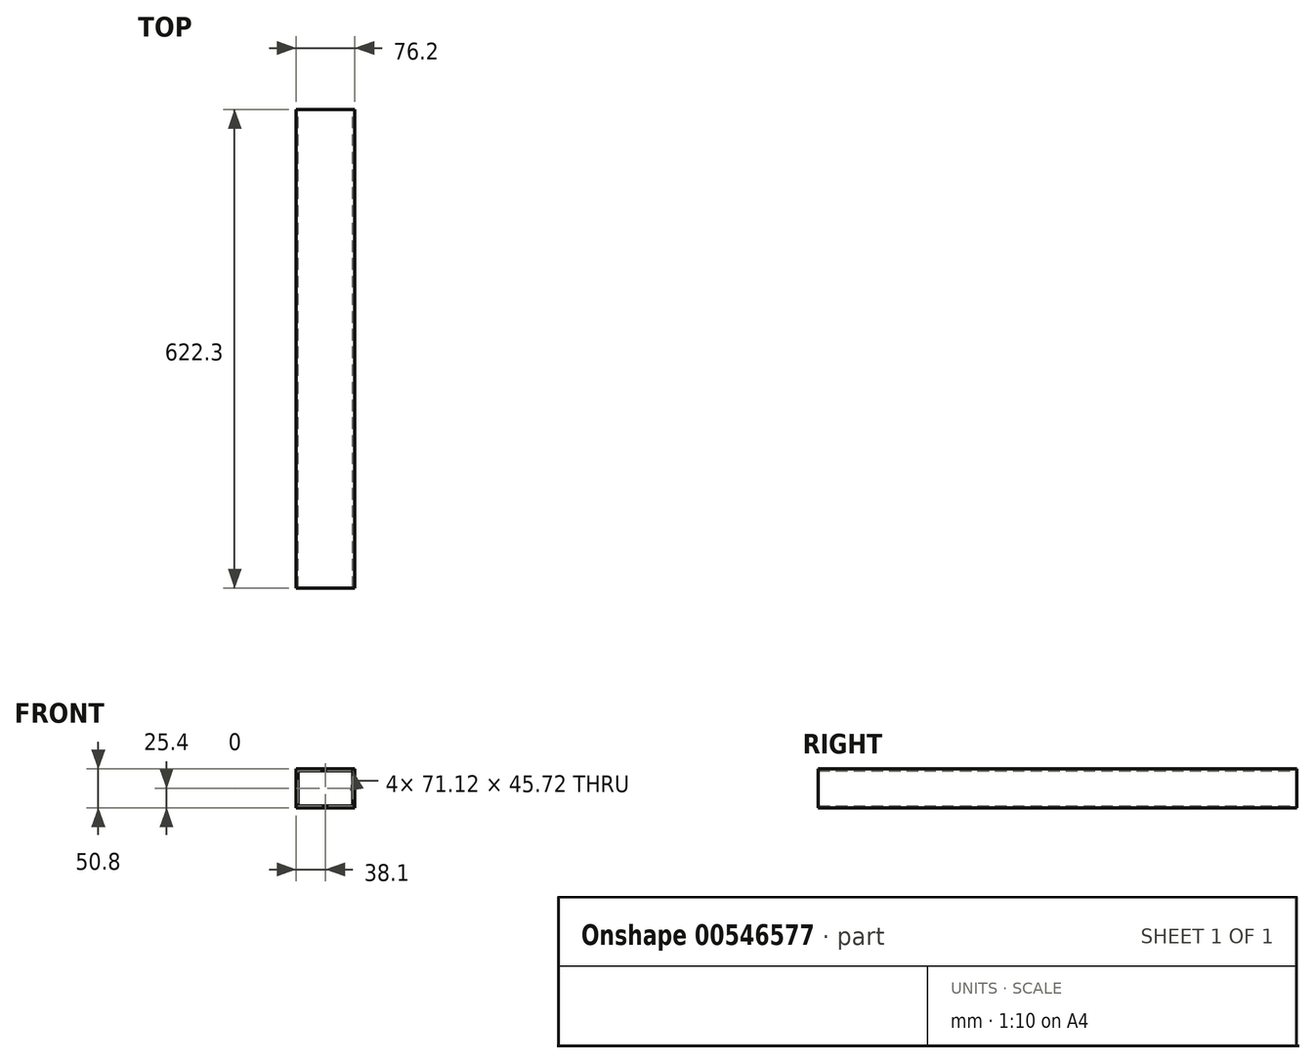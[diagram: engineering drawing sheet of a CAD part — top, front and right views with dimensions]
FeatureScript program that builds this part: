
annotation { "Feature Type Name" : "Feature", "Feature Type Description" : "" }
export const myFeature = defineFeature(function(context is Context, id is Id, definition is map)
    precondition{}
    {
        {
            var Q0;
            Q0=qCreatedBy(makeId("Front.planeOp"),FACE);
            var sketch = newSketch(context, id + "F0", { "sketchPlane" : qUnion([Q0])});
            skLineSegment(sketch, "E0.bottom", {"start": v(38.1, 25.4) * mm, "end": v(-38.1, 25.4) * mm});
            skLineSegment(sketch, "E0.top", {"start": v(38.1, -25.4) * mm, "end": v(-38.1, -25.4) * mm});
            skLineSegment(sketch, "E0.left", {"start": v(38.1, 25.4) * mm, "end": v(38.1, -25.4) * mm});
            skLineSegment(sketch, "E0.right", {"start": v(-38.1, 25.4) * mm, "end": v(-38.1, -25.4) * mm});
            skPoint(sketch, "E0.middle", {"position": v(0, 0) * mm});
            skSolve(sketch);
        }
        {
            var Q0;
            Q0=makeQuery(id+"F0.imprint","IMPRINT",FACE,{"disambiguationData":[TD([[makeQuery(id+"F0.imprint","IMPRINT",EDGE,{"derivedFrom":sQuery(id+"F0.wireOp",EDGE,"E0.bottom")}),1.0]])]});
            extrude(context, id + "F1", {"entities" : qUnion([Q0]), "depth" : 622.3 * mm, "offsetDistance" : 25.4 * mm});
        }
        {
            var Q0;
            Q0=makeQuery(id+"F1.opExtrude","CAP_FACE",FACE,{"disambiguationData":[OSD([sQuery(id+"F0.wireOp",EDGE,"E0.bottom"),sQuery(id+"F0.wireOp",EDGE,"E0.top"),sQuery(id+"F0.wireOp",EDGE,"E0.left"),sQuery(id+"F0.wireOp",EDGE,"E0.right")])],"isStart":true});
            var Q1;
            Q1=makeQuery(id+"F1.opExtrude","CAP_FACE",FACE,{"disambiguationData":[OSD([sQuery(id+"F0.wireOp",EDGE,"E0.bottom"),sQuery(id+"F0.wireOp",EDGE,"E0.top"),sQuery(id+"F0.wireOp",EDGE,"E0.left"),sQuery(id+"F0.wireOp",EDGE,"E0.right")])],"isStart":false});
            shell(context, id + "F2", {"entities" : qUnion([Q0, Q1]), "thickness" : 2.54 * mm});
        }
    });
